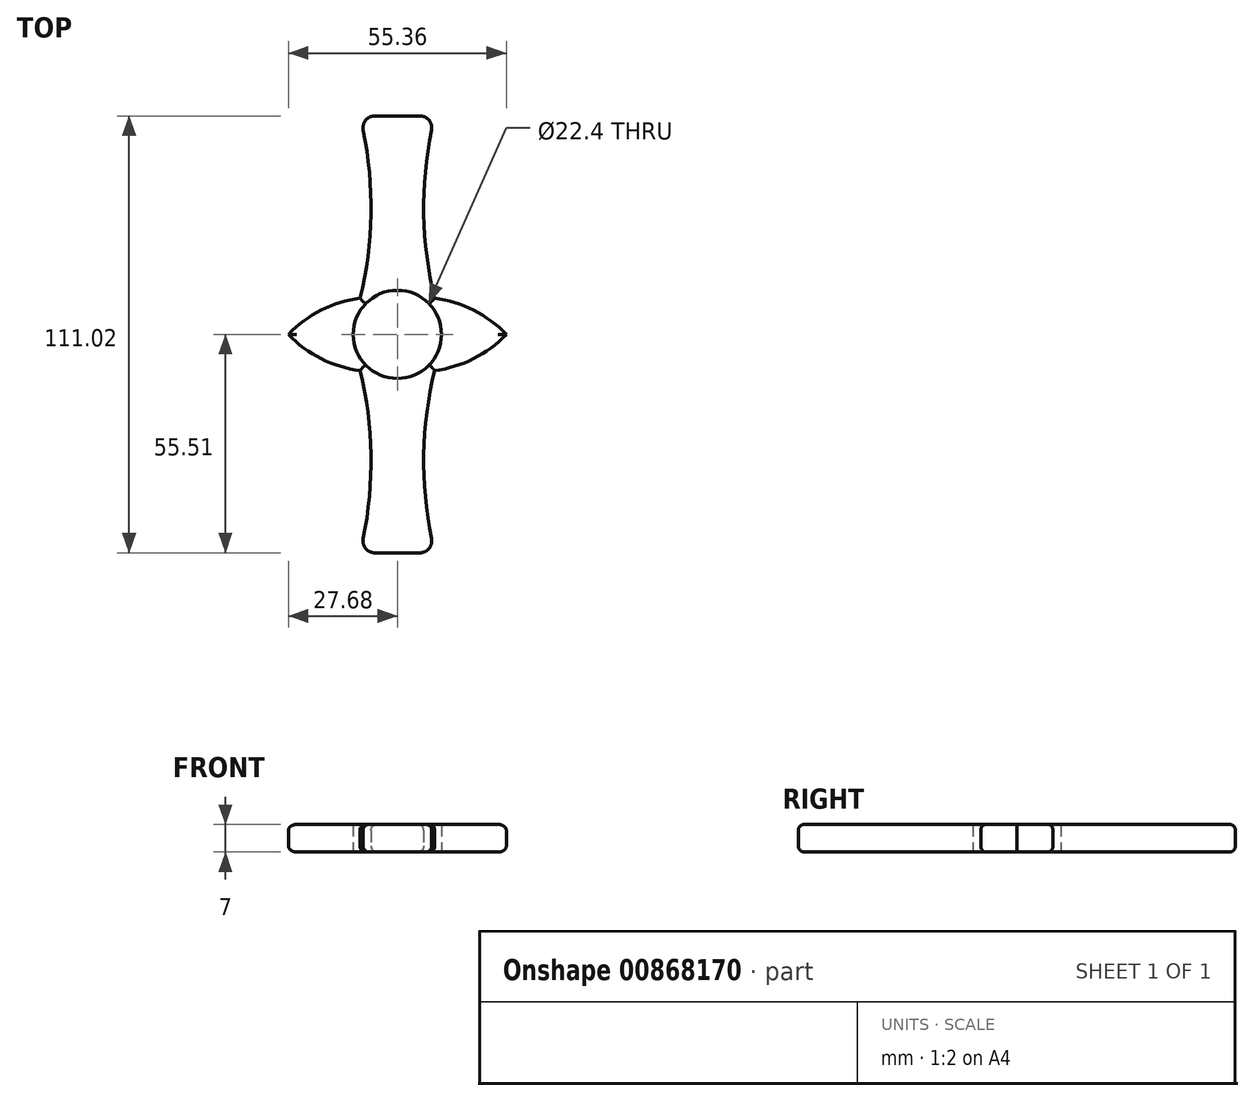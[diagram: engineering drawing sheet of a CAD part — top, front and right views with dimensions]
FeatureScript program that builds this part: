
annotation { "Feature Type Name" : "Feature", "Feature Type Description" : "" }
export const myFeature = defineFeature(function(context is Context, id is Id, definition is map)
    precondition{}
    {
        {
            var Q0;
            Q0=qCreatedBy(makeId("Top.planeOp"),FACE);
            var sketch = newSketch(context, id + "F0", { "sketchPlane" : qUnion([Q0])});
            skCircle(sketch, "E0", {"center": v(0, 0) * mm, "radius": 11.2 * mm});
            skArc(sketch, "E1", {"start": v(8.67, 51.91) * mm, "mid": v(6.71, 30.5) * mm, "end": v(9.47, 9.2) * mm});
            skArc(sketch, "E2.MirrorCS", {"start": v(-8.67, 51.91) * mm, "mid": v(-6.71, 30.5) * mm, "end": v(-9.47, 9.2) * mm});
            skPoint(sketch, "E3.MirrorCS.end.orphan", {"position": v(-9.47, 55.5) * mm});
            skPoint(sketch, "E3.MirrorCS.start.orphan", {"position": v(-9.47, 9.2) * mm});
            skLineSegment(sketch, "E4", {"start": v(-5.73, 55.5) * mm, "end": v(5.73, 55.5) * mm});
            skArc(sketch, "E5.filletArc", {"start": v(-5.73, 55.5) * mm, "mid": v(-8.05, 54.4) * mm, "end": v(-8.67, 51.91) * mm});
            skPoint(sketch, "E6.visualSharp", {"position": v(9.47, 55.5) * mm});
            skArc(sketch, "E6.filletArc", {"start": v(8.67, 51.91) * mm, "mid": v(8.05, 54.4) * mm, "end": v(5.73, 55.5) * mm});
            skArc(sketch, "E7.1.0", {"start": v(5.73, -55.5) * mm, "mid": v(8.05, -54.4) * mm, "end": v(8.67, -51.91) * mm});
            skArc(sketch, "E7.1.1", {"start": v(-8.67, -51.91) * mm, "mid": v(-8.05, -54.4) * mm, "end": v(-5.73, -55.5) * mm});
            skLineSegment(sketch, "E7.1.2", {"start": v(5.73, -55.5) * mm, "end": v(-5.73, -55.5) * mm});
            skArc(sketch, "E7.1.3", {"start": v(8.67, -51.91) * mm, "mid": v(6.71, -30.5) * mm, "end": v(9.47, -9.2) * mm});
            skArc(sketch, "E7.1.4", {"start": v(-8.67, -51.91) * mm, "mid": v(-6.71, -30.5) * mm, "end": v(-9.47, -9.2) * mm});
            skArc(sketch, "E8", {"start": v(-9.47, 9.2) * mm, "mid": v(-19.37, 6.17) * mm, "end": v(-27.68, 0) * mm});
            skArc(sketch, "E9.MirrorCS", {"start": v(-9.47, -9.2) * mm, "mid": v(-19.37, -6.17) * mm, "end": v(-27.68, 0) * mm});
            skArc(sketch, "E10.MirrorCS", {"start": v(9.47, 9.2) * mm, "mid": v(19.37, 6.17) * mm, "end": v(27.68, 0) * mm});
            skArc(sketch, "E11.MirrorCS", {"start": v(9.47, -9.2) * mm, "mid": v(19.37, -6.17) * mm, "end": v(27.68, 0) * mm});
            skSolve(sketch);
        }
        {
            var Q0;
            Q0=makeQuery(id+"F0.imprint","IMPRINT",FACE,{"disambiguationData":[TD([[makeQuery(id+"F0.imprint","IMPRINT",EDGE,{"derivedFrom":sQuery(id+"F0.wireOp",EDGE,"E0")}),-1.0]])]});
            extrude(context, id + "F1", {"entities" : qUnion([Q0]), "depth" : 7 * mm, "offsetDistance" : 25 * mm});
        }
        {
            var Q0;
            Q0=makeQuery(id+"F1.opExtrude","CAP_EDGE",EDGE,{"disambiguationData":[OSD([sQuery(id+"F0.wireOp",EDGE,"E7.1.3")])],"isStart":false});
            var Q1;
            Q1=makeQuery(id+"F1.opExtrude","CAP_EDGE",EDGE,{"disambiguationData":[OSD([sQuery(id+"F0.wireOp",EDGE,"E7.1.4")])],"isStart":false});
            var Q2;
            Q2=makeQuery(id+"F1.opExtrude","CAP_EDGE",EDGE,{"disambiguationData":[OSD([sQuery(id+"F0.wireOp",EDGE,"E2.MirrorCS")])],"isStart":false});
            var Q3;
            Q3=makeQuery(id+"F1.opExtrude","CAP_EDGE",EDGE,{"disambiguationData":[OSD([sQuery(id+"F0.wireOp",EDGE,"E4")])],"isStart":false});
            var Q4;
            Q4=makeQuery(id+"F1.opExtrude","CAP_EDGE",EDGE,{"disambiguationData":[OSD([sQuery(id+"F0.wireOp",EDGE,"E1")])],"isStart":false});
            var Q5;
            Q5=makeQuery(id+"F1.opExtrude","CAP_EDGE",EDGE,{"disambiguationData":[OSD([sQuery(id+"F0.wireOp",EDGE,"E10.MirrorCS")])],"isStart":false});
            var Q6;
            Q6=makeQuery(id+"F1.opExtrude","CAP_EDGE",EDGE,{"disambiguationData":[OSD([sQuery(id+"F0.wireOp",EDGE,"E11.MirrorCS")])],"isStart":false});
            var Q7;
            Q7=makeQuery(id+"F1.opExtrude","CAP_EDGE",EDGE,{"disambiguationData":[OSD([sQuery(id+"F0.wireOp",EDGE,"E8")])],"isStart":false});
            var Q8;
            Q8=makeQuery(id+"F1.opExtrude","CAP_EDGE",EDGE,{"disambiguationData":[OSD([sQuery(id+"F0.wireOp",EDGE,"E9.MirrorCS")])],"isStart":false});
            var Q9;
            Q9=makeQuery(id+"F1.opExtrude","CAP_EDGE",EDGE,{"disambiguationData":[OSD([sQuery(id+"F0.wireOp",EDGE,"E7.1.2")])],"isStart":false});
            fillet(context, id + "F2", {"entities" : qUnion([Q0, Q1, Q2, Q3, Q4, Q5, Q6, Q7, Q8, Q9]), "radius" : 1.5 * mm, "tangentPropagation" : true, "allowEdgeOverflow" : false});
        }
        {
            var Q0;
            Q0=makeQuery(id+"F1.opExtrude","CAP_EDGE",EDGE,{"disambiguationData":[OSD([sQuery(id+"F0.wireOp",EDGE,"E7.1.2")])],"isStart":true});
            var Q1;
            Q1=makeQuery(id+"F1.opExtrude","CAP_EDGE",EDGE,{"disambiguationData":[OSD([sQuery(id+"F0.wireOp",EDGE,"E7.1.0")])],"isStart":true});
            var Q2;
            Q2=makeQuery(id+"F1.opExtrude","CAP_EDGE",EDGE,{"disambiguationData":[OSD([sQuery(id+"F0.wireOp",EDGE,"E9.MirrorCS")])],"isStart":true});
            var Q3;
            Q3=makeQuery(id+"F1.opExtrude","CAP_EDGE",EDGE,{"disambiguationData":[OSD([sQuery(id+"F0.wireOp",EDGE,"E8")])],"isStart":true});
            var Q4;
            Q4=makeQuery(id+"F1.opExtrude","CAP_EDGE",EDGE,{"disambiguationData":[OSD([sQuery(id+"F0.wireOp",EDGE,"E2.MirrorCS")])],"isStart":true});
            var Q5;
            Q5=makeQuery(id+"F1.opExtrude","CAP_EDGE",EDGE,{"disambiguationData":[OSD([sQuery(id+"F0.wireOp",EDGE,"E1")])],"isStart":true});
            var Q6;
            Q6=makeQuery(id+"F1.opExtrude","CAP_EDGE",EDGE,{"disambiguationData":[OSD([sQuery(id+"F0.wireOp",EDGE,"E10.MirrorCS")])],"isStart":true});
            var Q7;
            Q7=makeQuery(id+"F1.opExtrude","CAP_EDGE",EDGE,{"disambiguationData":[OSD([sQuery(id+"F0.wireOp",EDGE,"E11.MirrorCS")])],"isStart":true});
            fillet(context, id + "F3", {"entities" : qUnion([Q0, Q1, Q2, Q3, Q4, Q5, Q6, Q7]), "radius" : 1.5 * mm, "tangentPropagation" : true, "allowEdgeOverflow" : false});
        }
    });
